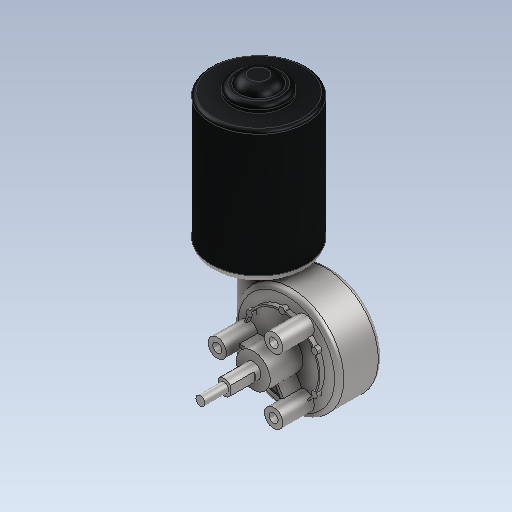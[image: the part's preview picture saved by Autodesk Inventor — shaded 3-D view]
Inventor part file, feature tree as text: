
AUTODESK INVENTOR PART (.ipt)
format: ipt  version: 2021 (Build 250183000, 183)  size: 381,440 bytes
history: native  units: in
note: dims shown in document units (in); Inventor stores cm internally (conversion verified against a paired STEP export)
features: sketch x7, other x3
ambient origin geometry x8: Origin, YZ Plane, XZ Plane, XY Plane, X Axis, Y Axis, Z Axis, Center Point
bodies: Solid1 (feature_tree)
feature tree (10):
  other  "motor_left.ipt"
  other  "Solid1::motor_left.ipt"
  other  "TaggingFeature1"
  sketch  "Sketch1"  dims[d0=0.3937in]
  sketch  "Sketch2"
  sketch  "Sketch3"
  sketch  "Sketch4"
  sketch  "Sketch5"
  sketch  "Sketch6"
  sketch  "Sketch7"
